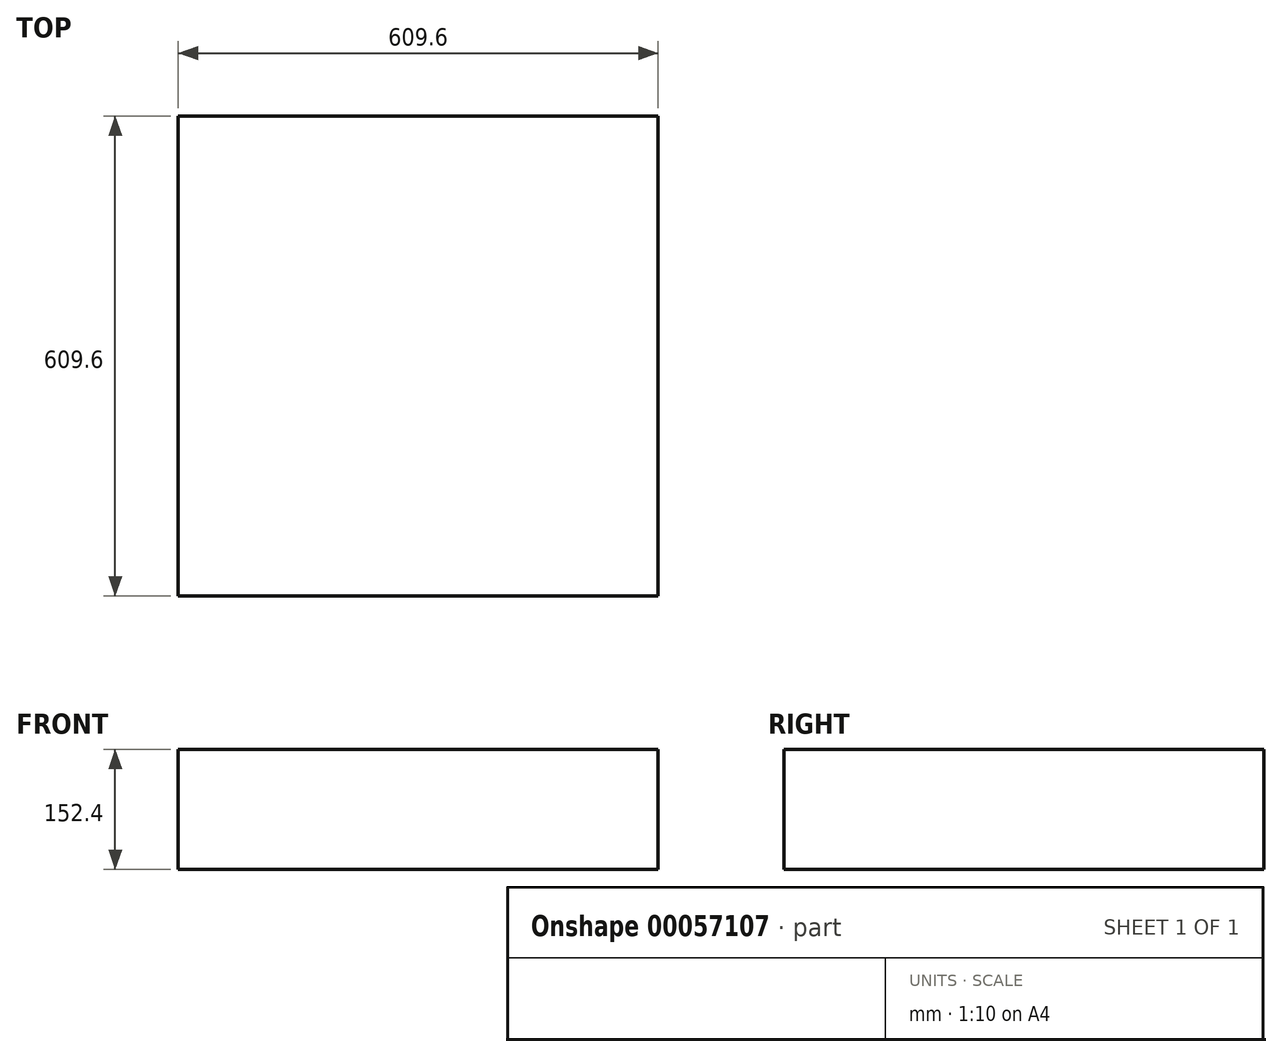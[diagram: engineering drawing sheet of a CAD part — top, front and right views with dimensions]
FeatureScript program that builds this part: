
annotation { "Feature Type Name" : "Feature", "Feature Type Description" : "" }
export const myFeature = defineFeature(function(context is Context, id is Id, definition is map)
    precondition{}
    {
        {
            var Q0;
            Q0=qCreatedBy(makeId("Top.planeOp"),FACE);
            var sketch = newSketch(context, id + "F0", { "sketchPlane" : qUnion([Q0])});
            skLineSegment(sketch, "E0.rect.bottom", {"start": v(313.91, 304.8) * mm, "end": v(-295.69, 304.8) * mm});
            skLineSegment(sketch, "E0.rect.top", {"start": v(313.91, -304.8) * mm, "end": v(-295.69, -304.8) * mm});
            skLineSegment(sketch, "E0.rect.left", {"start": v(313.91, 304.8) * mm, "end": v(313.91, -304.8) * mm});
            skLineSegment(sketch, "E0.rect.right", {"start": v(-295.69, 304.8) * mm, "end": v(-295.69, -304.8) * mm});
            skPoint(sketch, "E0.rect.middle", {"position": v(9.11, 0) * mm});
            skSolve(sketch);
        }
        {
            var Q0;
            Q0=makeQuery(id+"F0.imprint","IMPRINT",FACE,{"disambiguationData":[TD([[makeQuery(id+"F0.imprint","IMPRINT",EDGE,{"derivedFrom":sQuery(id+"F0.wireOp",EDGE,"E0.rect.bottom")}),1.0]])]});
            extrude(context, id + "F1", {"entities" : qUnion([Q0]), "oppositeDirection" : true, "depth" : 152.4 * mm});
        }
    });
